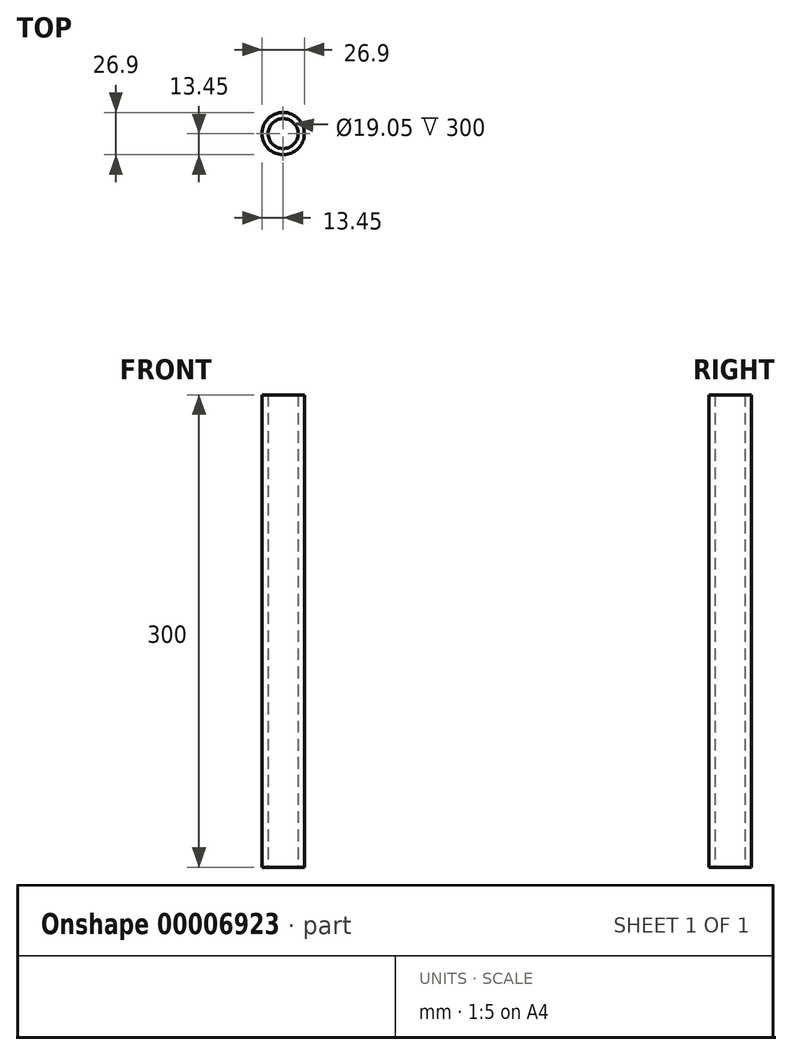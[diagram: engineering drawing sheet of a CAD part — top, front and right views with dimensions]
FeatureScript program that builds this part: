
annotation { "Feature Type Name" : "Feature", "Feature Type Description" : "" }
export const myFeature = defineFeature(function(context is Context, id is Id, definition is map)
    precondition{}
    {
        {
            var Q0;
            Q0=qCreatedBy(makeId("Top.planeOp"),FACE);
            var sketch = newSketch(context, id + "F0", { "sketchPlane" : qUnion([Q0])});
            skCircle(sketch, "E0", {"center": v(0, 0) * mm, "radius": 13.45 * mm});
            skCircle(sketch, "E1", {"center": v(0, 0) * mm, "radius": 9.53 * mm});
            skSolve(sketch);
        }
        {
            var Q0;
            Q0 = qSketchRegion(id + "F0", true);
            extrude(context, id + "F1", {"entities" : qUnion([Q0]), "depth" : 300 * mm});
        }
    });
